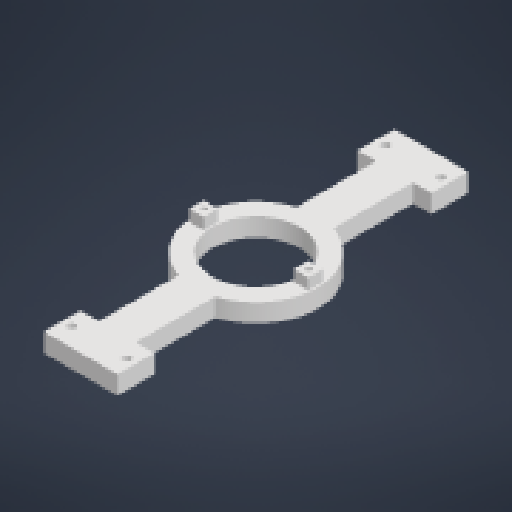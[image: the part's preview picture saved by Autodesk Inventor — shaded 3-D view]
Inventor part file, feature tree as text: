
AUTODESK INVENTOR PART (.ipt)
format: ipt  version: 2023.2 (Build 272271000, 271)  size: 191,488 bytes
history: native  units: in
note: dims shown in document units (in); Inventor stores cm internally (conversion verified against a paired STEP export)
features: extrude x6, sketch x6
ambient origin geometry x8: Origin, YZ Plane, XZ Plane, XY Plane, X Axis, Y Axis, Z Axis, Center Point
bodies: Solid1 (feature_tree)
feature tree (12):
  extrude  "Extrusion1"  Depth=7.4803in
  extrude  "Extrusion2"  Depth=0.7874in
  extrude  "Extrusion3"  Depth=0.7874in
  extrude  "Extrusion4"  Depth=0.3937in
  extrude  "Extrusion5"  Depth=0.3937in TaperAngle=0.0deg
  extrude  "Extrusion6"  Depth=0.7874in
  sketch  "Sketch1"  dims[d0=0.7874in d1=7.4803in]
  sketch  "Sketch2"  dims[d2=1.5748in d3=0.7874in]
  sketch  "Sketch3"  dims[d4=1.5748in d5=0.7874in]
  sketch  "Sketch4"  dims[d6=0.3937in d7=0.0in d8=1.8504in]
  sketch  "Sketch5"  dims[d9=2.6378in d10=0.3937in d11=0.0in]
  sketch  "Sketch6"  dims[d12=0.3937in d13=0.0in d14=0.1575in d15=0.1575in d16=0.1575in d17=0.1575in d18=0.3937in d19=0.0in d20=0.315in d21=0.315in d22=0.7874in d24=360.0deg d26=0.2362in d27=0.0in d28=0.1181in d29=0.7874in d31=360.0deg d33=0.0in d34=0.0in]
